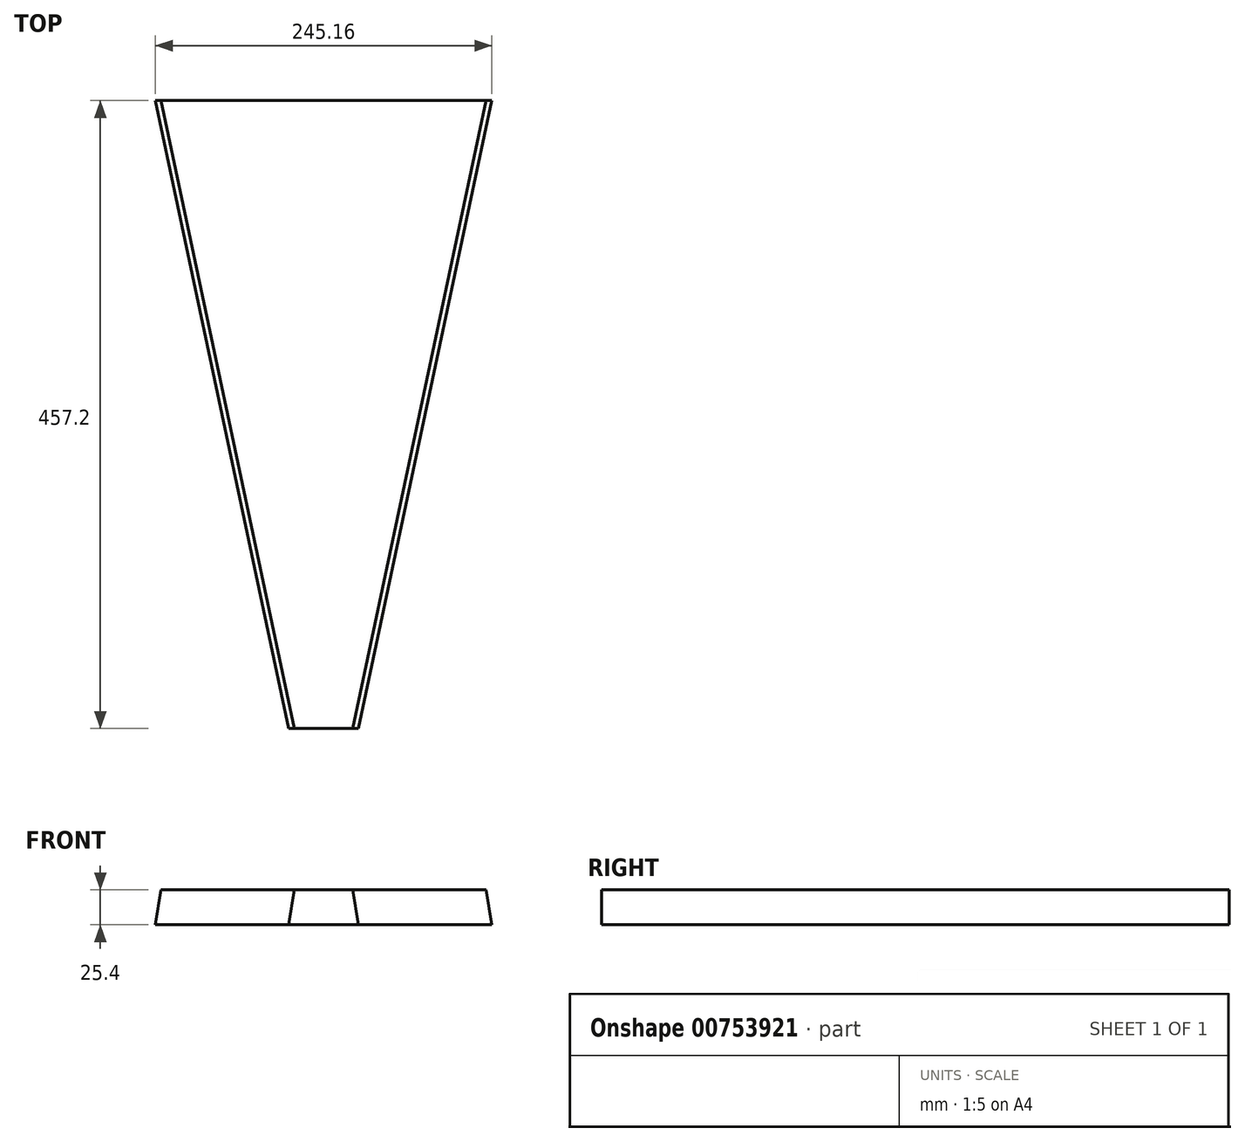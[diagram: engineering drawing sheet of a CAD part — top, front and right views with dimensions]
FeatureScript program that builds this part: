
annotation { "Feature Type Name" : "Feature", "Feature Type Description" : "" }
export const myFeature = defineFeature(function(context is Context, id is Id, definition is map)
    precondition{}
    {
        {
            assignVariable(context, id + "F0", {"name" : "Chamfer", "anyValue" : 9});
        }
        {
            var Q0;
            Q0=qCreatedBy(makeId("Top.planeOp"),FACE);
            var sketch = newSketch(context, id + "F1", { "sketchPlane" : qUnion([Q0])});
            skLineSegment(sketch, "E0", {"start": v(-25.4, 0) * mm, "end": v(25.4, 0) * mm});
            skLineSegment(sketch, "E1", {"start": v(25.4, 0) * mm, "end": v(122.58, 457.2) * mm});
            skLineSegment(sketch, "E2", {"start": v(122.58, 457.2) * mm, "end": v(-122.58, 457.2) * mm});
            skLineSegment(sketch, "E3", {"start": v(-122.58, 457.2) * mm, "end": v(-25.4, 0) * mm});
            skLineSegment(sketch, "E4", {"start": v(0, 0) * mm, "end": v(0, 457.2) * mm, "construction": true});
            skSolve(sketch);
        }
        {
            var Q0;
            Q0 = qSketchRegion(id + "F1", true);
            extrude(context, id + "F2", {"entities" : qUnion([Q0]), "depth" : 25.4 * mm, "offsetDistance" : 25.4 * mm});
        }
        {
            var Q0;
            Q0=makeQuery(id+"F2.opExtrude","CAP_EDGE",EDGE,{"disambiguationData":[OSD([sQuery(id+"F1.wireOp",EDGE,"E3")])],"isStart":false});
            var Q1;
            Q1=makeQuery(id+"F2.opExtrude","CAP_EDGE",EDGE,{"disambiguationData":[OSD([sQuery(id+"F1.wireOp",EDGE,"E1")])],"isStart":false});
            chamfer(context, id + "F3", {"entities" : qUnion([Q0, Q1]), "chamferType" : ChamferType.OFFSET_ANGLE, "width" : 25.4 * mm, "oppositeDirection" : true, "angle" : (getVariable(context, 'Chamfer')) * degree, "tangentPropagation" : true});
        }
    });
